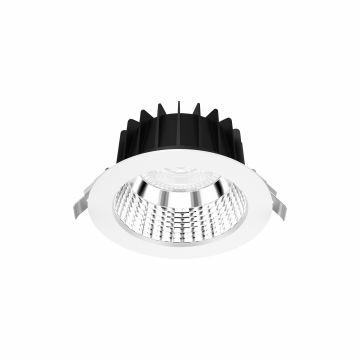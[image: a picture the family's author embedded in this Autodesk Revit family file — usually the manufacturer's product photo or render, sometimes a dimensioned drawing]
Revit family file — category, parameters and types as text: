
# Revit family: Lighting-Terziario-GEWISS-ELIA-AL-LED_INCASSO_ACCENTO_D145
name_source: partatom
category: Apparecchi per illuminazione
units: mm (PartAtom-declared; Revit-internal decimal feet)

## family parameters
Condiviso = No
Host = Superficie
Punto di calcolo locali = Sì
Quota connettore circolare = Usa diametro
Sorgente d'illuminazione = Sì
Taglio con vuoti quando caricato = No
Tipo di parte = Normale

## types (16) — shared parameters
Angolo inclinazione = -90.00°
Applicazione = Interno
Catalogo = LIGHTING
Catalogo Serie = ELIA AL
Classe isolamento = II
Colore = Bianco
Dimensioni (mm) = Standard
Emetti da lunghezza linea = 610 mm
FORO_CONTROSOFFITTO = 80 mm  [stored 0.262467 ft]
File diagramma fotometrico = GWF1411GH940.IES
Filtro dei colori = 16777215
Garanzia = 5 anni
Grado di protezione = IP40 - IP54
IDF = 41421456-b9f5-47ea-8ba5-c5c0e50a6ac9
IDT = 40448338-f630-44a4-b37d-0c013efb62a7
Immagine tipo = ELIA_AL.jpg
Installazione = Incasso modulare
LARGHEZZA_FORO = 820 mm
LED = <Per categoria>
LED Life time (L80B50) = L80 B50 (Tq25°) = 50.000h
LUNGHEZZA FORO = 969 mm
L_lampada = 1500 mm
Lampada: = LED
POSIZIONE = 80000
Peso (kg) = 0,5
Peso (kg): = 0,5
Potenza di sistema = 18W
Produttore = GEWISS S.p.A.
Prospetto di default = 1219 mm
Resistenza agli urti = IK06
SEO = Incasso modulare
STRUTTURA = <Per categoria>
Scheda Tecnica = https://www.gewiss.com
Temperatura di funzionamento = -20° +45°
Temperatura di utilizzo = -20° +45°
Tensione = 220-240 VÂ
Tipo lampada = LED
Tipologia = Incasso modulare
Tipologia sorgente luminosa = LED - Non sostituibile
UGR: = UGR<19
URL = https://www.gewiss.com
Variazione temperatura colore lampada con luminosità attenuata = <Nessuno>
Versione file RFA = 20.0

## per-type parameters (varying)
| type | Descrizione | Lumen output (lm) | Modello | Ottica | Temperatura di colore | Temperatura di colore: |
| GWF1410GH940 - ELIA AL S2 40K 60° ST.ALONE ON/OFF CRI90 | ELIA AL S2 40K 60° ST.ALONE ON/OFF CRI90 | 1900 | GWF1410GH940 | 60° | 4000K | 4000K |
| GWF1410GG830 - ELIA AL S2 30K 36° ST.ALONE ON/OFF CRI80 | ELIA AL S2 30K 36° ST.ALONE ON/OFF CRI80 | 1900 | GWF1410GG830 | 36° | 3000K | 3000K |
| GWF1411GH930 - ELIA AL S2 30K 60° ST.ALONE DALI CRI90 | ELIA AL S2 30K 60° ST.ALONE DALI CRI90 | 1790 | GWF1411GH930 | 60° | 3000K | 3000K |
| GWF1410GG840 - ELIA AL S2 40K 36° ST.ALONE ON/OFF CRI80 | ELIA AL S2 40K 36° ST.ALONE ON/OFF CRI80 | 2030 | GWF1410GG840 | 36° | 4000K | 4000K |
| GWF1410GG930 - ELIA AL S2 30K 36° ST.ALONE ON/OFF CRI90 | ELIA AL S2 30K 36° ST.ALONE ON/OFF CRI90 | 1700 | GWF1410GG930 | 36° | 3000K | 3000K |
| GWF1410GG940 - ELIA AL S2 40K 36° ST.ALONE ON/OFF CRI90 | ELIA AL S2 40K 36° ST.ALONE ON/OFF CRI90 | 1800 | GWF1410GG940 | 36° | 4000K | 4000K |
| GWF1411GG940 - ELIA AL S2 40K 36° ST.ALONE DALI CRI90 | ELIA AL S2 40K 36° ST.ALONE DALI CRI90 | 1800 | GWF1411GG940 | 36° | 4000K | 4000K |
| GWF1410GH830 - ELIA AL S2 30K 60° ST.ALONE ON/OFF CRI80 | ELIA AL S2 30K 60° ST.ALONE ON/OFF CRI80 | 1990 | GWF1410GH830 | 60° | 3000K | 3000K |
| GWF1411GG830 - ELIA AL S2 30K 36° ST.ALONE DALI CRI80 | ELIA AL S2 30K 36° ST.ALONE DALI CRI80 | 1900 | GWF1411GG830 | 36° | 3000K | 3000K |
| GWF1410GH930 - ELIA AL S2 30K 60° ST.ALONE ON/OFF CRI90 | ELIA AL S2 30K 60° ST.ALONE ON/OFF CRI90 | 1790 | GWF1410GH930 | 60° | 3000K | 3000K |
| GWF1411GH830 - ELIA AL S2 30K 60° ST.ALONE DALI CRI80 | ELIA AL S2 30K 60° ST.ALONE DALI CRI80 | 1990 | GWF1411GH830 | 60° | 3000K | 3000K |
| GWF1411GG930 - ELIA AL S2 30K 36° ST.ALONE DALI CRI90 | ELIA AL S2 30K 36° ST.ALONE DALI CRI90 | 1700 | GWF1411GG930 | 36° | 3000K | 3000K |
| GWF1411GH840 - ELIA AL S2 40K 60° ST.ALONE DALI CRI80 | ELIA AL S2 40K 60° ST.ALONE DALI CRI80 | 2120 | GWF1411GH840 | 60° | 4000K | 4000K |
| GWF1410GH840 - ELIA AL S2 40K 60° ST.ALONE ON/OFF CRI80 | ELIA AL S2 40K 60° ST.ALONE ON/OFF CRI80 | 2120 | GWF1410GH840 | 60° | 4000K | 4000K |
| GWF1411GG840 - ELIA AL S2 40K 36° ST.ALONE DALI CRI80 | ELIA AL S2 40K 36° ST.ALONE DALI CRI80 | 2030 | GWF1411GG840 | 36° | 4000K | 4000K |
| GWF1411GH940 - ELIA AL S2 40K 60° ST.ALONE DALI CRI90 | ELIA AL S2 40K 60° ST.ALONE DALI CRI90 | 1900 | GWF1411GH940 | 60° | 4000K | 4000K |

note: [stored X ft] marks values corroborated as IEEE doubles in the binary element streams (Revit-internal decimal feet)
